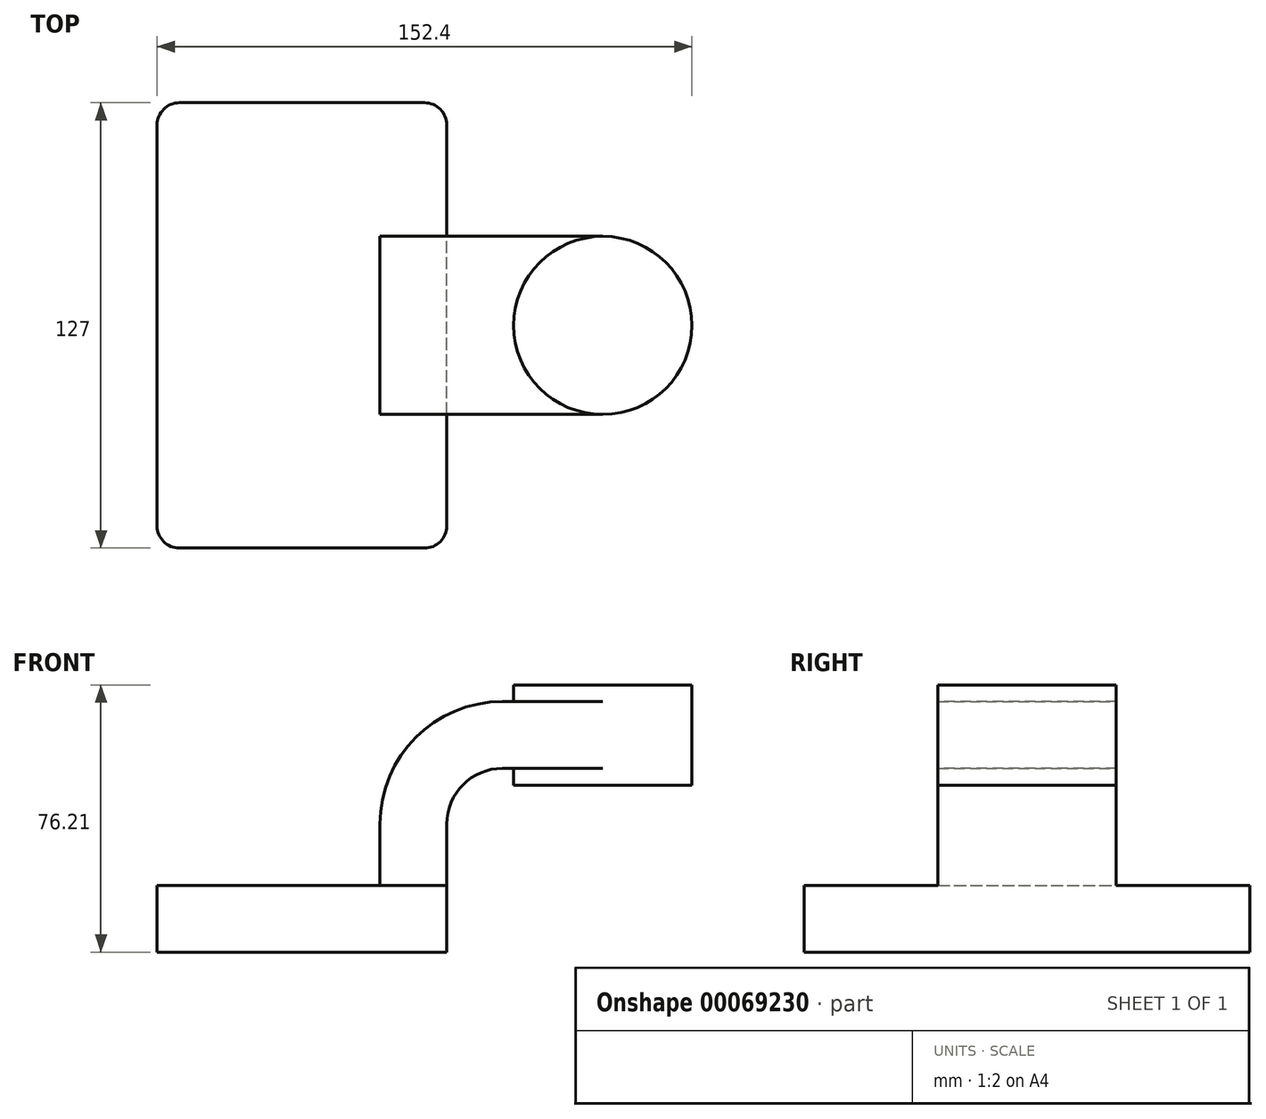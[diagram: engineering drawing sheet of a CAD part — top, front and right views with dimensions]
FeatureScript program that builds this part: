
annotation { "Feature Type Name" : "Feature", "Feature Type Description" : "" }
export const myFeature = defineFeature(function(context is Context, id is Id, definition is map)
    precondition{}
    {
        {
            var Q0;
            Q0=qCreatedBy(makeId("Front.planeOp"),FACE);
            var sketch = newSketch(context, id + "F0", { "sketchPlane" : qUnion([Q0])});
            skLineSegment(sketch, "E0.rect.bottom", {"start": v(41.27, 9.53) * mm, "end": v(-41.28, 9.53) * mm});
            skLineSegment(sketch, "E0.rect.top", {"start": v(41.28, -9.52) * mm, "end": v(-41.28, -9.52) * mm});
            skLineSegment(sketch, "E0.rect.left", {"start": v(41.28, 9.53) * mm, "end": v(41.28, -9.52) * mm});
            skLineSegment(sketch, "E0.rect.right", {"start": v(-41.28, 9.53) * mm, "end": v(-41.28, -9.52) * mm});
            skPoint(sketch, "E0.rect.middle", {"position": v(0, 0) * mm});
            skLineSegment(sketch, "E1.rect.bottom", {"start": v(111.12, 38.1) * mm, "end": v(60.32, 38.1) * mm});
            skLineSegment(sketch, "E1.rect.top", {"start": v(111.12, 66.68) * mm, "end": v(60.32, 66.68) * mm});
            skLineSegment(sketch, "E1.rect.left", {"start": v(111.12, 38.1) * mm, "end": v(111.12, 66.68) * mm});
            skLineSegment(sketch, "E1.rect.right", {"start": v(60.32, 38.1) * mm, "end": v(60.32, 66.68) * mm});
            skPoint(sketch, "E1.rect.middle", {"position": v(85.72, 52.39) * mm});
            skLineSegment(sketch, "E2", {"start": v(41.27, 9.53) * mm, "end": v(41.27, 27) * mm});
            skArc(sketch, "E3", {"start": v(41.27, 27) * mm, "mid": v(45.92, 38.23) * mm, "end": v(57.15, 42.88) * mm});
            skLineSegment(sketch, "E4", {"start": v(57.15, 42.88) * mm, "end": v(85.72, 42.88) * mm});
            skLineSegment(sketch, "E5.0", {"start": v(57.15, 61.93) * mm, "end": v(85.72, 61.93) * mm});
            skArc(sketch, "E5.1", {"start": v(22.22, 27) * mm, "mid": v(32.45, 51.7) * mm, "end": v(57.15, 61.93) * mm});
            skLineSegment(sketch, "E5.2", {"start": v(22.22, 9.53) * mm, "end": v(22.22, 27) * mm});
            skLineSegment(sketch, "E6", {"start": v(85.72, 66.68) * mm, "end": v(85.72, 38.1) * mm});
            skFitSpline(sketch, "E7", {"points": [v(-41.28, 9.53) * mm, v(57.15, 61.93) * mm], "startDerivative": vector(1.32, 84.02) * mm, "endDerivative": vector(171.45, -0.42) * mm});
            skSolve(sketch);
        }
        {
            var Q0;
            Q0=makeQuery(id+"F0.imprint","IMPRINT",FACE,{"disambiguationData":[TD([[makeQuery(id+"F0.imprint","IMPRINT",EDGE,{"derivedFrom":sQuery(id+"F0.wireOp",EDGE,"E0.rect.top")}),-1.0]])]});
            extrude(context, id + "F1", {"entities" : qUnion([Q0]), "endBound" : BoundingType.SYMMETRIC, "depth" : 127 * mm});
        }
        {
            var Q0;
            {var subQ1=sQuery(id+"F0.wireOp",EDGE,"E2");Q0=makeQuery(id+"F0.imprint","IMPRINT",FACE,{"disambiguationData":[TD([[makeQuery(id+"F0.imprint","IMPRINT",EDGE,{"derivedFrom":subQ1}),1.0]])]});}
            var Q1;
            {var subQ0=sQuery(id+"F0.wireOp",EDGE,"E4");var subQ1=sQuery(id+"F0.wireOp",EDGE,"E1.rect.right");var subQ2=makeQuery(id+"F0.imprint","INTERSECT",VERTEX,{"derivedFrom":[subQ1,subQ0]});Q1=makeQuery(id+"F0.imprint","IMPRINT",FACE,{"disambiguationData":[TD([[makeQuery(id+"F0.imprint","IMPRINT",EDGE,{"disambiguationData":[TD([[subQ2,-1.0]])],"derivedFrom":subQ1}),-1.0]])]});}
            extrude(context, id + "F2", {"entities" : qUnion([Q0, Q1]), "operationType" : NewBodyOperationType.ADD, "endBound" : BoundingType.SYMMETRIC, "depth" : 50.8 * mm});
        }
        {
            var Q0;
            Q0=makeQuery(id+"F0.imprint","IMPRINT",FACE,{"disambiguationData":[TD([[makeQuery(id+"F0.imprint","IMPRINT",EDGE,{"derivedFrom":sQuery(id+"F0.wireOp",EDGE,"E5.1")}),1.0]])]});
            extrude(context, id + "F3", {"entities" : qUnion([Q0]), "operationType" : NewBodyOperationType.ADD, "endBound" : BoundingType.SYMMETRIC, "depth" : 15.88 * mm});
        }
        {
            var Q0;
            {var subQ0=sQuery(id+"F0.wireOp",EDGE,"E1.rect.left");Q0=makeQuery(id+"F0.imprint","IMPRINT",FACE,{"disambiguationData":[TD([[makeQuery(id+"F0.imprint","IMPRINT",EDGE,{"derivedFrom":subQ0}),1.0]])]});}
            var Q1;
            Q1=sQuery(id+"F0.wireOp",EDGE,"E6");
            revolve(context, id + "F4", {"operationType" : NewBodyOperationType.ADD, "entities" : qUnion([Q0]), "axis" : qUnion([Q1]), "revolveType" : RevolveType.FULL});
        }
        {
            var Q0;
            Q0=makeQuery(id+"F1.opExtrude","CAP_EDGE",EDGE,{"disambiguationData":[OSD([sQuery(id+"F0.wireOp",EDGE,"E0.rect.left")])],"isStart":false});
            var Q1;
            Q1=makeQuery(id+"F1.opExtrude","CAP_EDGE",EDGE,{"disambiguationData":[OSD([sQuery(id+"F0.wireOp",EDGE,"E0.rect.right")])],"isStart":false});
            var Q2;
            Q2=makeQuery(id+"F1.opExtrude","CAP_EDGE",EDGE,{"disambiguationData":[OSD([sQuery(id+"F0.wireOp",EDGE,"E0.rect.left")])],"isStart":true});
            var Q3;
            Q3=makeQuery(id+"F1.opExtrude","CAP_EDGE",EDGE,{"disambiguationData":[OSD([sQuery(id+"F0.wireOp",EDGE,"E0.rect.right")])],"isStart":true});
            fillet(context, id + "F5", {"entities" : qUnion([Q0, Q1, Q2, Q3]), "radius" : 6.35 * mm, "tangentPropagation" : true, "allowEdgeOverflow" : false});
        }
    });
